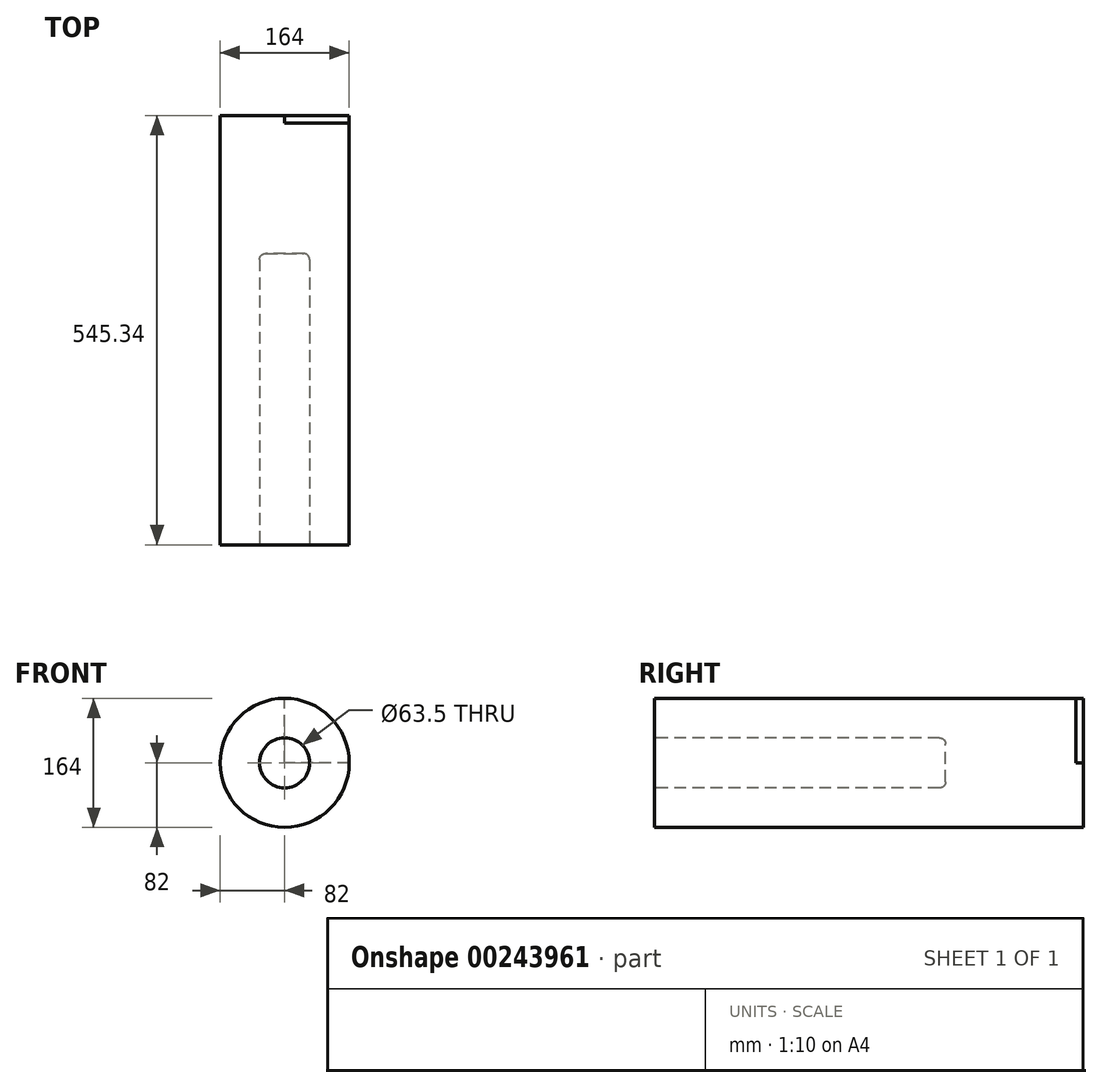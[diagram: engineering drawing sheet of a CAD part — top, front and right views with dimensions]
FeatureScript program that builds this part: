
annotation { "Feature Type Name" : "Feature", "Feature Type Description" : "" }
export const myFeature = defineFeature(function(context is Context, id is Id, definition is map)
    precondition{}
    {
        {
            var Q0;
            Q0=qCreatedBy(makeId("Front.planeOp"),FACE);
            var sketch = newSketch(context, id + "F0", { "sketchPlane" : qUnion([Q0])});
            skCircle(sketch, "E0", {"center": v(0, 0) * mm, "radius": 82 * mm});
            skSolve(sketch);
        }
        {
            var Q0;
            Q0 = qSketchRegion(id + "F0", true);
            extrude(context, id + "F1", {"entities" : qUnion([Q0]), "depth" : 545.34 * mm});
        }
        {
            var Q0;
            Q0=makeQuery(id+"F1.opExtrude","CAP_FACE",FACE,{"disambiguationData":[OSD([sQuery(id+"F0.wireOp",EDGE,"E0")])],"isStart":false});
            var sketch = newSketch(context, id + "F2", { "sketchPlane" : qUnion([Q0])});
            skCircle(sketch, "E1", {"center": v(0, 0) * mm, "radius": 31.75 * mm});
            skSolve(sketch);
        }
        {
            var Q0;
            Q0 = qSketchRegion(id + "F2", true);
            extrude(context, id + "F3", {"entities" : qUnion([Q0]), "operationType" : NewBodyOperationType.REMOVE, "oppositeDirection" : true, "depth" : 370.08 * mm});
        }
        {
            var Q0;
            Q0=makeQuery(id+"F3.boolean.opBoolean","COPY",EDGE,{"derivedFrom":makeQuery(id+"F3.opExtrude","CAP_EDGE",EDGE,{"disambiguationData":[OSD([sQuery(id+"F2.wireOp",EDGE,"E1")])],"isStart":false})});
            fillet(context, id + "F4", {"entities" : qUnion([Q0]), "radius" : 7.62 * mm, "tangentPropagation" : true, "allowEdgeOverflow" : false});
        }
        {
            var Q0;
            Q0=qCreatedBy(makeId("Right.planeOp"),FACE);
            var sketch = newSketch(context, id + "F5", { "sketchPlane" : qUnion([Q0])});
            skLineSegment(sketch, "E2.bottom", {"start": v(0, 0) * mm, "end": v(-9.83, 0) * mm});
            skLineSegment(sketch, "E2.top", {"start": v(0, 91.06) * mm, "end": v(-9.83, 91.06) * mm});
            skLineSegment(sketch, "E2.left", {"start": v(0, 0) * mm, "end": v(0, 91.06) * mm});
            skLineSegment(sketch, "E2.right", {"start": v(-9.83, 0) * mm, "end": v(-9.83, 91.06) * mm});
            skSolve(sketch);
        }
        {
            var Q0;
            Q0 = qSketchRegion(id + "F5", true);
            extrude(context, id + "F6", {"entities" : qUnion([Q0]), "operationType" : NewBodyOperationType.REMOVE, "depth" : 117 * mm});
        }
    });
